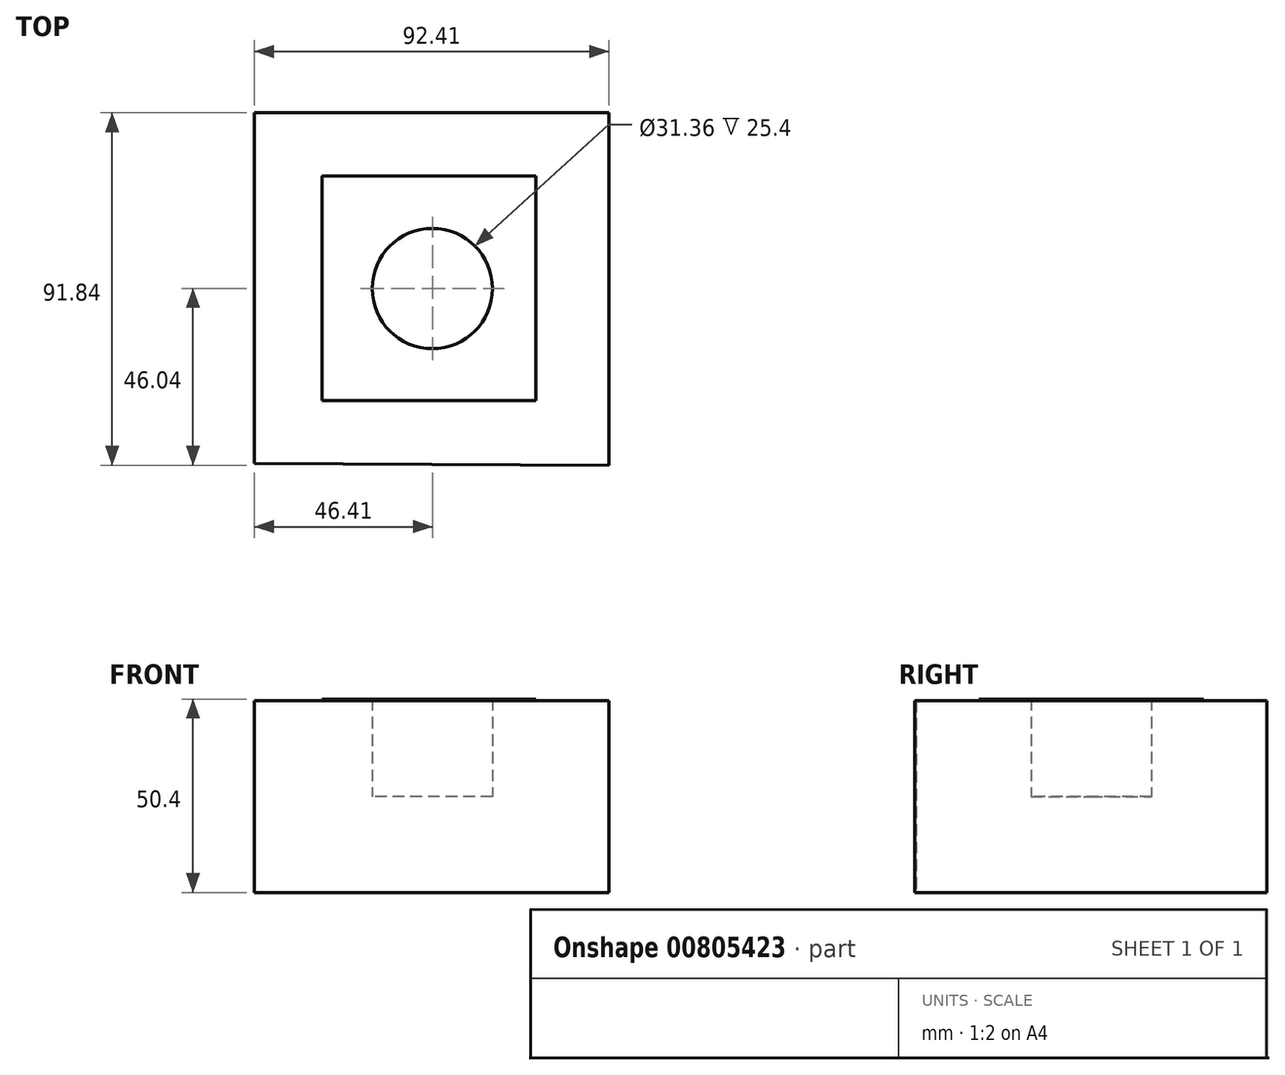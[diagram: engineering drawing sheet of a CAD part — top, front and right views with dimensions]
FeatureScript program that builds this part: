
annotation { "Feature Type Name" : "Feature", "Feature Type Description" : "" }
export const myFeature = defineFeature(function(context is Context, id is Id, definition is map)
    precondition{}
    {
        {
            var Q0;
            Q0=qCreatedBy(makeId("Top.planeOp"),FACE);
            var sketch = newSketch(context, id + "F0", { "sketchPlane" : qUnion([Q0])});
            skLineSegment(sketch, "E0.bottom", {"start": v(27.03, 29.37) * mm, "end": v(-28.75, 29.37) * mm});
            skLineSegment(sketch, "E0.top", {"start": v(27.03, -29.22) * mm, "end": v(-28.75, -29.22) * mm});
            skLineSegment(sketch, "E0.left", {"start": v(27.03, 29.37) * mm, "end": v(27.03, -29.22) * mm});
            skLineSegment(sketch, "E0.right", {"start": v(-28.75, 29.37) * mm, "end": v(-28.75, -29.22) * mm});
            skCircle(sketch, "E1", {"center": v(0, 0) * mm, "radius": 15.68 * mm});
            skSolve(sketch);
        }
        {
            var Q0;
            Q0=makeQuery(id+"F0.imprint","IMPRINT",FACE,{"disambiguationData":[TD([[makeQuery(id+"F0.imprint","IMPRINT",EDGE,{"derivedFrom":sQuery(id+"F0.wireOp",EDGE,"E0.bottom")}),1.0]])]});
            extrude(context, id + "F1", {"entities" : qUnion([Q0]), "depth" : 25.4 * mm, "offsetDistance" : 25.4 * mm});
        }
        {
            var Q0;
            Q0=qCreatedBy(makeId("Top.planeOp"),FACE);
            var sketch = newSketch(context, id + "F2", { "sketchPlane" : qUnion([Q0])});
            skLineSegment(sketch, "E2", {"start": v(27.02, -29.2) * mm, "end": v(46, -46.04) * mm});
            skLineSegment(sketch, "E3", {"start": v(46, -46.04) * mm, "end": v(46, 45.8) * mm});
            skLineSegment(sketch, "E4", {"start": v(46, 45.8) * mm, "end": v(-46.41, 45.8) * mm});
            skLineSegment(sketch, "E5", {"start": v(46, 45.8) * mm, "end": v(26.94, 29.5) * mm});
            skLineSegment(sketch, "E6", {"start": v(-46.41, 45.8) * mm, "end": v(-28.62, 29.23) * mm});
            skLineSegment(sketch, "E7", {"start": v(-46.41, 45.8) * mm, "end": v(-46.41, -45.6) * mm});
            skLineSegment(sketch, "E8", {"start": v(-46.41, -45.6) * mm, "end": v(-28.43, -29.25) * mm});
            skLineSegment(sketch, "E9", {"start": v(-46.41, -45.6) * mm, "end": v(46, -46.04) * mm});
            skSolve(sketch);
        }
        {
            var Q0;
            Q0=makeQuery(id+"F2.imprint","IMPRINT",FACE,{"disambiguationData":[TD([[makeQuery(id+"F2.imprint","IMPRINT",EDGE,{"derivedFrom":sQuery(id+"F2.wireOp",EDGE,"E3")}),1.0]])]});
            extrude(context, id + "F3", {"entities" : qUnion([Q0]), "operationType" : NewBodyOperationType.ADD, "depth" : 25 * mm, "offsetDistance" : 25 * mm});
        }
        {
            var Q0;
            Q0=makeQuery(id+"F1.opExtrude","CAP_FACE",FACE,{"disambiguationData":[OSD([sQuery(id+"F0.wireOp",EDGE,"E0.bottom"),sQuery(id+"F0.wireOp",EDGE,"E0.top"),sQuery(id+"F0.wireOp",EDGE,"E0.left"),sQuery(id+"F0.wireOp",EDGE,"E0.right"),sQuery(id+"F0.wireOp",EDGE,"E1")])],"isStart":false});
            var Q1;
            {var subQ0=sQuery(id+"F2.wireOp",EDGE,"E3");var subQ1=sQuery(id+"F2.wireOp",EDGE,"E4");var subQ2=sQuery(id+"F2.wireOp",EDGE,"E7");var subQ3=sQuery(id+"F2.wireOp",EDGE,"E9");Q1=makeQuery(id+"F3.boolean.opBoolean","SPLIT",FACE,{"disambiguationData":[TD([makeQuery(id+"F1.opExtrude","SWEPT_FACE",FACE,{"disambiguationData":[OSD([sQuery(id+"F0.wireOp",EDGE,"E0.bottom")])]})])],"derivedFrom":makeQuery(id+"F3.opExtrude","CAP_FACE",FACE,{"disambiguationData":[OSD([subQ0,subQ1,subQ2,subQ3])],"isStart":false})});}
            extrude(context, id + "F4", {"entities" : qUnion([Q0, Q1]), "operationType" : NewBodyOperationType.ADD, "depth" : 25 * mm, "offsetDistance" : 25 * mm});
        }
    });
